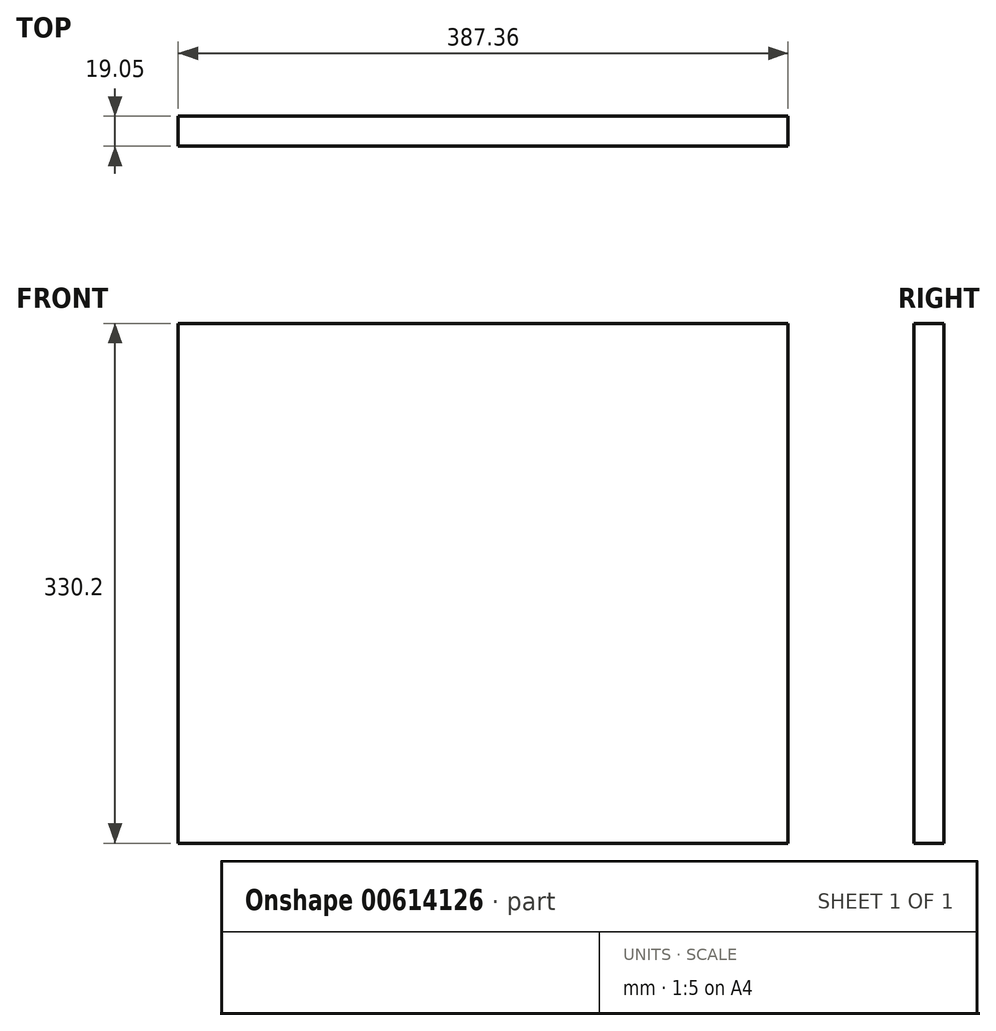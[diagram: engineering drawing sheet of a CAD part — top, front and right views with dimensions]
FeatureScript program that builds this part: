
annotation { "Feature Type Name" : "Feature", "Feature Type Description" : "" }
export const myFeature = defineFeature(function(context is Context, id is Id, definition is map)
    precondition{}
    {
        {
            var Q0;
            Q0=qCreatedBy(makeId("Front.planeOp"),FACE);
            var sketch = newSketch(context, id + "F0", { "sketchPlane" : qUnion([Q0])});
            skLineSegment(sketch, "E0.bottom", {"start": v(-193.68, 165.1) * mm, "end": v(193.68, 165.1) * mm});
            skLineSegment(sketch, "E0.top", {"start": v(-193.68, -165.1) * mm, "end": v(193.67, -165.1) * mm});
            skLineSegment(sketch, "E0.left", {"start": v(-193.68, 165.1) * mm, "end": v(-193.68, -165.1) * mm});
            skLineSegment(sketch, "E0.right", {"start": v(193.68, 165.1) * mm, "end": v(193.67, -165.1) * mm});
            skPoint(sketch, "E0.middle", {"position": v(0, 0) * mm});
            skSolve(sketch);
        }
        {
            var Q0;
            Q0=makeQuery(id+"F0.imprint","IMPRINT",FACE,{"disambiguationData":[TD([[makeQuery(id+"F0.imprint","IMPRINT",EDGE,{"derivedFrom":sQuery(id+"F0.wireOp",EDGE,"E0.bottom")}),-1.0]])]});
            extrude(context, id + "F1", {"entities" : qUnion([Q0]), "depth" : 19.05 * mm, "offsetDistance" : 25.4 * mm});
        }
    });
